# Revit family: Plumbing_Valves_TOTO-USA-Inc_EcoPowerR-High-Efficiency-Concealed-Toil
name_source: partatom
category: Plumbing Fixtures
revit_build: Autodesk Revit 2015 (Build: 20140606_1530(x64)
units: mm (PartAtom-declared; Revit-internal decimal feet)

## types (1)
- TET2LA31
    Ambient Temp. = 32°-104°F (0°-40°C)
    BIMobject category = Valves
    BIMobject category code = plumbing-valves
    BIMobject main category = Plumbing
    BIMobject main category code = plumbing
    Brand url = https://www.totousa.com
    Description = The water-powered turbine in the EcoPower flush valve charges the power supply during usage and provides maximum performance in even the most demanding, high-traffic commercial spaces.
    Discharge Quantity = Preset to 1.28 GPF/4.8 LPF
    Edition number = 1
    IFC Classification = Valve
    Installation instructions = https://www.totousa.com
    Manufacturer = TOTO
    Manufacturer name = TOTO USA Inc
    Material = Metal - TOTO - Stainless Steel
    Material main = Stainless steel
    Model = TET2LA31
    NBS Reference Code = 35-93-80
    NBS Reference Description = Urinal Flushing Valves
    Nominal height = 0 mm  [stored 0 ft]
    Nominal width = 0 mm  [stored 0 ft]
    OmniClass Code = 23-27 31 00
    OmniClass Description = Valves
    Product Guid = 28d91bff-0fa4-44d7-905a-d1d9b708375c
    Product SKU = toto-tet2la31
    Product certification = https://www.totousa.com
    Product data url = https://bimobject.com
    Product family = Toilet and Bath Specialties
    Product group = EcoPower??
    Product url = https://www.totousa.com
    QR code = http://bimobject.com
    Sensor Detection Range = Self-adjusting to environment
    Sensor Detection Time = Factory setting at six (6) seconds minimum
    Technical description = https://www.totousa.com
    UNSPSC Code = 401416
    URL = www.totousa.com
    Uniclass 1.4 Code = L7136
    Uniclass 1.4 Description = Valves
    Uniclass 2.0 Code = SS-35-65-90
    Uniclass 2.0 Description = Toilet Systems
    Uniclass 2015 Code = Pr_40_20_93_79
    Uniclass 2015 Name = Urinal flushing valves
    Warranty = Three year limited
    Water Supply Pressure(Max) = 861844.6 Pa
    Water Supply Pressure(Min) = 103421.4 Pa

note: [stored X ft] marks values corroborated as IEEE doubles in the binary element streams (Revit-internal decimal feet)

## geometry (parser evidence)
native form markers: Blend x4, Sweep x2
no freeform markers — native parametric forms only
